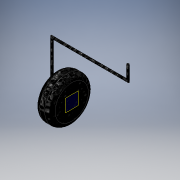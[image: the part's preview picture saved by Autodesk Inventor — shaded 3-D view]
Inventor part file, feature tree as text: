
AUTODESK INVENTOR PART (.ipt)
format: ipt  version: 2018 (Build 220112000, 112)  size: 137,728 bytes
history: native  units: in
note: dims shown in document units (in); Inventor stores cm internally (conversion verified against a paired STEP export)
features: sketch x3, plane x1, extrude x1, fillet x1, sweep x1
ambient origin geometry x8: Origin, YZ Plane, XZ Plane, XY Plane, X Axis, Y Axis, Z Axis, Center Point
bodies: Solid1 (feature_tree)
feature tree (7):
  sketch  "3D Sketch1"
  plane  "Work Plane1"
  extrude  "Extrusion1"  Depth=3.1496in
  fillet  "Fillet1"  Radius=5.1575in
  sweep  "Sweep1"
  sketch  "Sketch1"  dims[d0=1.3386in d1=3.1496in d2=5.1575in]
  sketch  "Sketch2"  dims[d3=0.9843in d4=2.9724in d5=1.0433in d6=0.0in d7=0.3543in d8=0.1575in d9=0.0in d10=0.0in]
